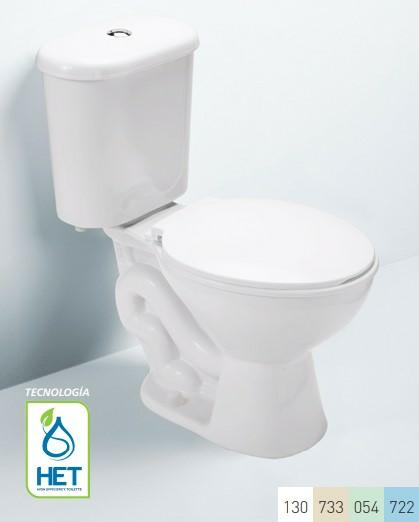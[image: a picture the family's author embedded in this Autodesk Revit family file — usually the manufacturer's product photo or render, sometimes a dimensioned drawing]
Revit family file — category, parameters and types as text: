
# Revit family: BRG-SNT-IOP-SANITARIO ONE PIECE_Kingsley Redondo blanco
name_source: partatom
category: Aparatos sanitarios
units: mm (PartAtom-declared; Revit-internal decimal feet)

## family parameters
Compartido = Sí
Corte con vacíos al cargar = No
Cota de conector redondo = Diámetro de uso
Número OmniClass = 23.45.00.00
Punto de cálculo de habitación = Sí
Se basa en plano de trabajo = No
Siempre vertical = Sí
Tipo de pieza = Normal
Título OmniClass = Sanitary, Laundry, and Cleaning Equipment

## types (1)
- KINGSLEY ADV REDONDO CON ASIENTO SLOW DOWN BLANCO
    Conexión AC = Sí
    Conexión AF = Sí
    Conexión de residuos = Sí
    Conexión de ventilación = Sí
    Fabricante = BRIGGS Ecuador
    Imagen de tipo = <Ninguno>
    Modelo = KINGSLEY ADV REDONDO CON ASIENTO SLOW DOWN BLANCO
    URL = https://www.briggs.com.ec
    _ALT_Basamento = 0.4 m
    _ALT_Eje instalación = 0.6 m
    _EDESA_ Alto en cm = 60.3
    _EDESA_ Ancho en cm = 49.8
    _EDESA_ Certificación = Cumple con norma NTE INEN 3082
    _EDESA_ Color = blanco
    _EDESA_ Consumo/capacidad de agua en L = 4.1 y 6.0 litros
    _EDESA_ Descripción = 0
    _EDESA_ Distancia de instalación en cm (muro terminado) = 30.5 cm
    _EDESA_ Manual de instalación = https://www.briggs.com.ec
    _EDESA_ Marca = BRIGGS
    _EDESA_ Nombre = INODORO KINGSLEY ADVANCE REDONDO CON ASIENTO SLOW DOWN BLANCO
    _EDESA_ Peso en kg = 40 kg
    _EDESA_ Productos incluídos = Asiento Crown slow down, Herraje dual flush, Botón Dual Flush Square, Set de Anclaje Taza Piso, Sello de Cera, Tapas de Anclaje. Productos Integrados incluye Llave angular para Inodoro con manguera de 12”
    _EDESA_ Productos necesarios para instalación = 0
    _EDESA_ Profundidad en cm = 70.6
    _EDESA_ Sku/código = JSSI60841301CB
    _EDESA_ Tipo de Aro = 0
    _EDESA_ Tipo de instalación = Al piso
